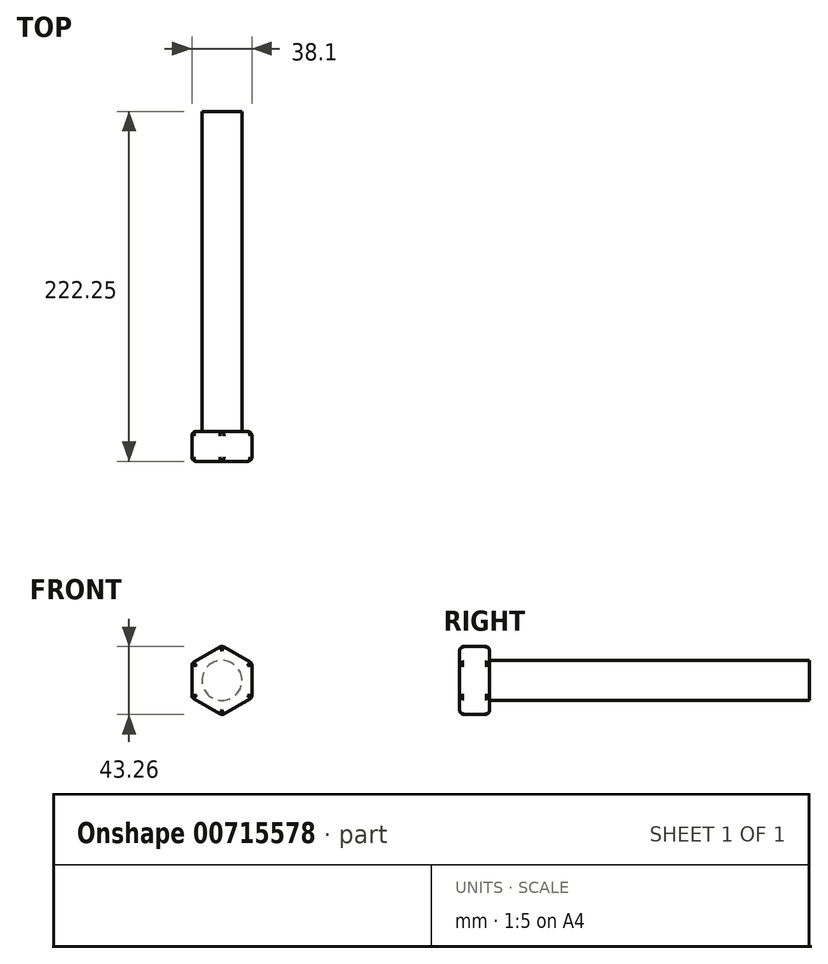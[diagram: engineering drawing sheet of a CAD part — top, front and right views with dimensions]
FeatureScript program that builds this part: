
annotation { "Feature Type Name" : "Feature", "Feature Type Description" : "" }
export const myFeature = defineFeature(function(context is Context, id is Id, definition is map)
    precondition{}
    {
        {
            var Q0;
            Q0=qCreatedBy(makeId("Front.planeOp"),FACE);
            var sketch = newSketch(context, id + "F0", { "sketchPlane" : qUnion([Q0])});
            skCircle(sketch, "E0", {"center": v(0, 0) * mm, "radius": 12.7 * mm});
            skSolve(sketch);
        }
        {
            var Q0;
            Q0 = qSketchRegion(id + "F0", true);
            extrude(context, id + "F1", {"entities" : qUnion([Q0]), "depth" : 203.2 * mm, "offsetDistance" : 25.4 * mm});
        }
        {
            var Q0;
            Q0=makeQuery(id+"F1.opExtrude","CAP_FACE",FACE,{"disambiguationData":[OSD([sQuery(id+"F0.wireOp",EDGE,"E0")])],"isStart":false});
            var sketch = newSketch(context, id + "F2", { "sketchPlane" : qUnion([Q0])});
            skCircle(sketch, "E1.cCircle", {"center": v(0, 0) * mm, "radius": 19.05 * mm, "construction": true});
            skLineSegment(sketch, "E1.0", {"start": v(19.05, 11) * mm, "end": v(19.05, -11) * mm});
            skLineSegment(sketch, "E1.1", {"start": v(19.05, -11) * mm, "end": v(0, -22) * mm});
            skLineSegment(sketch, "E1.2", {"start": v(0, -22) * mm, "end": v(-19.05, -11) * mm});
            skLineSegment(sketch, "E1.3", {"start": v(-19.05, -11) * mm, "end": v(-19.05, 11) * mm});
            skLineSegment(sketch, "E1.4", {"start": v(-19.05, 11) * mm, "end": v(0, 22) * mm});
            skLineSegment(sketch, "E1.5", {"start": v(0, 22) * mm, "end": v(19.05, 11) * mm});
            skPoint(sketch, "E1.0.midPoint", {"position": v(19.05, 0) * mm});
            skSolve(sketch);
        }
        {
            var Q0;
            Q0 = qSketchRegion(id + "F2", true);
            extrude(context, id + "F3", {"entities" : qUnion([Q0]), "operationType" : NewBodyOperationType.ADD, "depth" : 19.05 * mm, "offsetDistance" : 25.4 * mm});
        }
        {
            var Q0;
            Q0=makeQuery(id+"F3.opExtrude","SWEPT_EDGE",EDGE,{"disambiguationData":[OSD([sQuery(id+"F2.wireOp",EDGE,"E1.1"),sQuery(id+"F2.wireOp",EDGE,"E1.2")])]});
            var Q1;
            Q1=makeQuery(id+"F3.opExtrude","SWEPT_EDGE",EDGE,{"disambiguationData":[OSD([sQuery(id+"F2.wireOp",EDGE,"E1.0"),sQuery(id+"F2.wireOp",EDGE,"E1.1")])]});
            var Q2;
            Q2=makeQuery(id+"F3.opExtrude","SWEPT_EDGE",EDGE,{"disambiguationData":[OSD([sQuery(id+"F2.wireOp",EDGE,"E1.0"),sQuery(id+"F2.wireOp",EDGE,"E1.5")])]});
            var Q3;
            Q3=makeQuery(id+"F3.opExtrude","SWEPT_EDGE",EDGE,{"disambiguationData":[OSD([sQuery(id+"F2.wireOp",EDGE,"E1.4"),sQuery(id+"F2.wireOp",EDGE,"E1.5")])]});
            var Q4;
            Q4=makeQuery(id+"F3.opExtrude","SWEPT_EDGE",EDGE,{"disambiguationData":[OSD([sQuery(id+"F2.wireOp",EDGE,"E1.3"),sQuery(id+"F2.wireOp",EDGE,"E1.4")])]});
            var Q5;
            Q5=makeQuery(id+"F3.opExtrude","SWEPT_EDGE",EDGE,{"disambiguationData":[OSD([sQuery(id+"F2.wireOp",EDGE,"E1.2"),sQuery(id+"F2.wireOp",EDGE,"E1.3")])]});
            fillet(context, id + "F4", {"entities" : qUnion([Q0, Q1, Q2, Q3, Q4, Q5]), "radius" : 2.54 * mm, "rho" : 0.5, "crossSection" : FilletCrossSection.CONIC, "allowEdgeOverflow" : false});
        }
        {
            var Q0;
            {var subQ0=sQuery(id+"F2.wireOp",EDGE,"E1.3");var subQ1=sQuery(id+"F2.wireOp",EDGE,"E1.2");Q0=makeQuery(id+"F4.opFillet","BLEND_EDGE",EDGE,{"blendedFrom":[makeQuery(id+"F3.opExtrude","SWEPT_EDGE",EDGE,{"disambiguationData":[OSD([subQ1,subQ0])]}),makeQuery(id+"F3.opExtrude","CAP_FACE",FACE,{"disambiguationData":[OSD([sQuery(id+"F2.wireOp",EDGE,"E1.0"),sQuery(id+"F2.wireOp",EDGE,"E1.1"),subQ1,subQ0,sQuery(id+"F2.wireOp",EDGE,"E1.4"),sQuery(id+"F2.wireOp",EDGE,"E1.5")])],"isStart":false})],"blendedInto":[makeQuery(id+"F3.opExtrude","CAP_FACE",FACE,{"disambiguationData":[OSD([sQuery(id+"F2.wireOp",EDGE,"E1.0"),sQuery(id+"F2.wireOp",EDGE,"E1.1"),subQ1,subQ0,sQuery(id+"F2.wireOp",EDGE,"E1.4"),sQuery(id+"F2.wireOp",EDGE,"E1.5")])],"isStart":false})]});}
            var Q1;
            {var subQ0=sQuery(id+"F2.wireOp",EDGE,"E1.2");var subQ1=sQuery(id+"F2.wireOp",EDGE,"E1.1");Q1=makeQuery(id+"F4.opFillet","BLEND_EDGE",EDGE,{"blendedFrom":[makeQuery(id+"F3.opExtrude","SWEPT_EDGE",EDGE,{"disambiguationData":[OSD([subQ1,subQ0])]}),makeQuery(id+"F3.opExtrude","CAP_FACE",FACE,{"disambiguationData":[OSD([sQuery(id+"F2.wireOp",EDGE,"E1.0"),subQ1,subQ0,sQuery(id+"F2.wireOp",EDGE,"E1.3"),sQuery(id+"F2.wireOp",EDGE,"E1.4"),sQuery(id+"F2.wireOp",EDGE,"E1.5")])],"isStart":true})],"blendedInto":[makeQuery(id+"F3.opExtrude","CAP_FACE",FACE,{"disambiguationData":[OSD([sQuery(id+"F2.wireOp",EDGE,"E1.0"),subQ1,subQ0,sQuery(id+"F2.wireOp",EDGE,"E1.3"),sQuery(id+"F2.wireOp",EDGE,"E1.4"),sQuery(id+"F2.wireOp",EDGE,"E1.5")])],"isStart":true})]});}
            fillet(context, id + "F5", {"entities" : qUnion([Q0, Q1]), "radius" : 2.8 * mm, "tangentPropagation" : true, "allowEdgeOverflow" : false});
        }
    });
